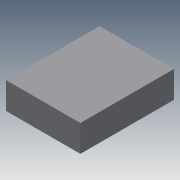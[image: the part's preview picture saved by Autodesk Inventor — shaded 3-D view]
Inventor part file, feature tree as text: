
AUTODESK INVENTOR PART (.ipt)
format: ipt  version: 2013 (Build 170138000, 138)  size: 67,584 bytes
history: native  units: mm
features: extrude x1, sketch x1
ambient origin geometry x8: Origin, YZ Plane, XZ Plane, XY Plane, X Axis, Y Axis, Z Axis, Center Point
bodies: Solid1 (feature_tree)
feature tree (2):
  extrude  "Extrusion1"  Depth=35.0mm
  sketch  "Sketch1"  dims[d0=27.8mm d1=35.0mm d2=10.0mm d3=0.0mm]
